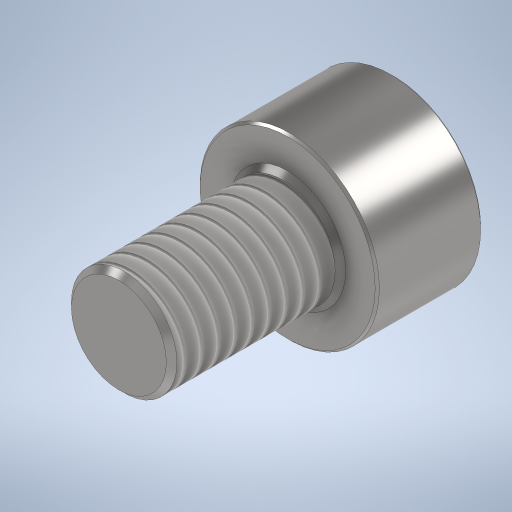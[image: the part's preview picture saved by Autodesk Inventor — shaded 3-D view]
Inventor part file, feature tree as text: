
AUTODESK INVENTOR PART (.ipt)
format: ipt  version: 2024 (Build 280153000, 153)  size: 332,288 bytes
history: native  units: mm
features: extrude x3, chamfer x3, sketch x2, thread x1, hole x1
ambient origin geometry x8: Origin, YZ Plane, XZ Plane, XY Plane, X Axis, Y Axis, Z Axis, Center Point
bodies: Solid1 (feature_tree)
feature tree (10):
  sketch  "Sketch1"  dims[d0=8.5mm d1=5.0mm]
  extrude  "Extrusion1"  Depth=5.0mm
  extrude  "Extrusion2"  Depth=2.5mm TaperAngle=0.0deg
  thread  "Thread1"  [1 undecoded]
  chamfer  "Chamfer1"  Distance=0.1mm Angle=45.0deg
  sketch  "Sketch2"  dims[d2=8.0mm d3=0.0mm d4=5.0mm d5=0.0mm d6=15.0mm d7=0.0mm d8=0.1mm d9=2.0mm d10=45.0deg d11=3.75mm d12=4.0mm d15=0.5mm d16=2.0mm d17=45.0deg d18=3.0mm d19=0.0mm d20=0.25mm d21=2.0mm d22=45.0deg d23=3.75mm d24=6.0mm d25=4.0mm d26=2.0mm d27=90.0deg d28=2.5mm d29=150.0deg]
  hole  "Hole1"  [1 undecoded]
  chamfer  "Chamfer2"  Distance=4.0mm
  extrude  "Extrusion4"  Depth=2.5mm TaperAngle=45.0deg
  chamfer  "Chamfer3"  Distance=3.0mm
note: 2 required parameter values undecoded (feature->parameter linkage not recoverable at this tier; creation-order binding heuristic only, values carry confidence <= 0.55)
